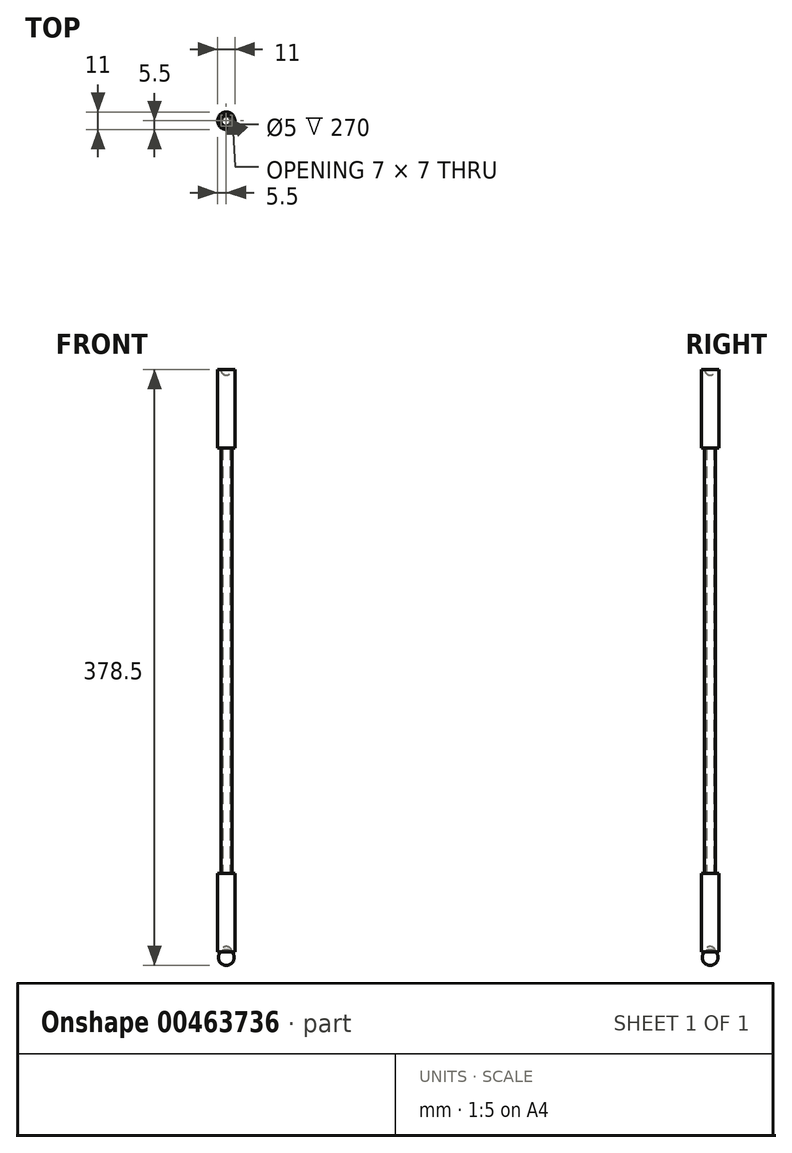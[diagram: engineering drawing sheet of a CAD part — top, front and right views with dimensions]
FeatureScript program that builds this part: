
annotation { "Feature Type Name" : "Feature", "Feature Type Description" : "" }
export const myFeature = defineFeature(function(context is Context, id is Id, definition is map)
    precondition{}
    {
        {
            var Q0;
            Q0=qCreatedBy(makeId("Top.planeOp"),FACE);
            var sketch = newSketch(context, id + "F0", { "sketchPlane" : qUnion([Q0])});
            skCircle(sketch, "E0", {"center": v(0, 0) * mm, "radius": 3.5 * mm});
            skCircle(sketch, "E1", {"center": v(0, 0) * mm, "radius": 2.5 * mm});
            skSolve(sketch);
        }
        {
            var Q0;
            Q0 = qSketchRegion(id + "F0", true);
            extrude(context, id + "F1", {"entities" : qUnion([Q0]), "flatOperationType" : FlatOperationType.REMOVE, "offsetDistance" : 25 * mm, "depth" : 300 * mm, "domain" : OperationDomain.MODEL});
        }
        {
            var Q0;
            Q0=makeQuery(id+"F1.opExtrude","CAP_FACE",FACE,{"disambiguationData":[OSD([sQuery(id+"F0.wireOp",EDGE,"E0"),sQuery(id+"F0.wireOp",EDGE,"E1")])],"isStart":true});
            var sketch = newSketch(context, id + "F2", { "sketchPlane" : qUnion([Q0])});
            skCircle(sketch, "E2", {"center": v(0, 0) * mm, "radius": 5.5 * mm});
            skSolve(sketch);
        }
        {
            var Q0;
            Q0 = qSketchRegion(id + "F2", true);
            extrude(context, id + "F3", {"entities" : qUnion([Q0]), "operationType" : NewBodyOperationType.ADD, "flatOperationType" : FlatOperationType.REMOVE, "offsetDistance" : 25 * mm, "depth" : 25 * mm, "hasSecondDirection" : true, "secondDirectionOppositeDirection" : true, "secondDirectionDepth" : 25 * mm, "domain" : OperationDomain.MODEL});
        }
        {
            var Q0;
            Q0=makeQuery(id+"F3.opExtrude","CAP_FACE",FACE,{"disambiguationData":[OSD([sQuery(id+"F2.wireOp",EDGE,"E2")])],"isStart":false});
            var sketch = newSketch(context, id + "F4", { "sketchPlane" : qUnion([Q0])});
            skLineSegment(sketch, "E3", {"start": v(0, -5.5) * mm, "end": v(0, 5.5) * mm});
            skCircle(sketch, "E4", {"center": v(0, 0) * mm, "radius": 3.5 * mm});
            skSolve(sketch);
        }
        {
            var Q0;
            {var subQ0=sQuery(id+"F4.wireOp",EDGE,"E4");var subQ1=sQuery(id+"F4.wireOp",EDGE,"E3");var subQ2=makeQuery(id+"F4.imprint","INTERSECT",VERTEX,{"disambiguationData":[OD(0.0)],"derivedFrom":[subQ1,subQ0]});Q0=makeQuery(id+"F4.imprint","IMPRINT",FACE,{"disambiguationData":[TD([[makeQuery(id+"F4.imprint","IMPRINT",EDGE,{"disambiguationData":[TD([[subQ2,-1.0]])],"derivedFrom":subQ1}),-1.0]])]});}
            var Q1;
            Q1=sQuery(id+"F4.wireOp",EDGE,"E3");
            revolve(context, id + "F5", {"operationType" : NewBodyOperationType.REMOVE, "entities" : qUnion([Q0]), "axis" : qUnion([Q1]), "revolveType" : RevolveType.FULL, "oppositeDirection" : true});
        }
        {
            var Q0;
            Q0=qCreatedBy(makeId("Right.planeOp"),FACE);
            var sketch = newSketch(context, id + "F6", { "sketchPlane" : qUnion([Q0])});
            skCircle(sketch, "E5", {"center": v(0, -28.5) * mm, "radius": 5 * mm});
            skLineSegment(sketch, "E6", {"start": v(0, -23.5) * mm, "end": v(0, -33.5) * mm});
            skLineSegment(sketch, "E7", {"start": v(0, -21.85) * mm, "end": v(0, -34.1) * mm});
            skSolve(sketch);
        }
        {
            var Q0;
            {var subQ0=sQuery(id+"F6.wireOp",EDGE,"E7");var subQ1=sQuery(id+"F6.wireOp",EDGE,"E5");var subQ2=makeQuery(id+"F6.imprint","INTERSECT",VERTEX,{"disambiguationData":[OD(0.0)],"derivedFrom":[subQ1,subQ0]});Q0=makeQuery(id+"F6.imprint","IMPRINT",FACE,{"disambiguationData":[TD([[makeQuery(id+"F6.imprint","IMPRINT",EDGE,{"disambiguationData":[TD([[subQ2,1.0]])],"derivedFrom":subQ1}),1.0]])]});}
            var Q1;
            Q1=sQuery(id+"F6.wireOp",EDGE,"E6");
            revolve(context, id + "F7", {"entities" : qUnion([Q0]), "axis" : qUnion([Q1]), "revolveType" : RevolveType.FULL});
        }
        {
            var Q0;
            Q0=qCreatedBy(makeId("Top.planeOp"),FACE);
            cPlane(context, id + "F8", {"entities" : qUnion([Q0]), "cplaneType" : CPlaneType.OFFSET, "offset" : 160 * mm, "width" : 150 * mm, "height" : 150 * mm});
        }
        {
            var Q0;
            Q0=makeQuery(id+"F1.opExtrude","SWEPT_BODY",BODY,{"disambiguationData":[OSD([sQuery(id+"F0.wireOp",EDGE,"E0"),sQuery(id+"F0.wireOp",EDGE,"E1")])]});
            var Q1;
            Q1=qCreatedBy(id+"F8.planeOp",FACE);
            mirror(context, id + "F9", {"operationType" : NewBodyOperationType.ADD, "entities" : qUnion([Q0]), "mirrorPlane" : qUnion([Q1])});
        }
    });
